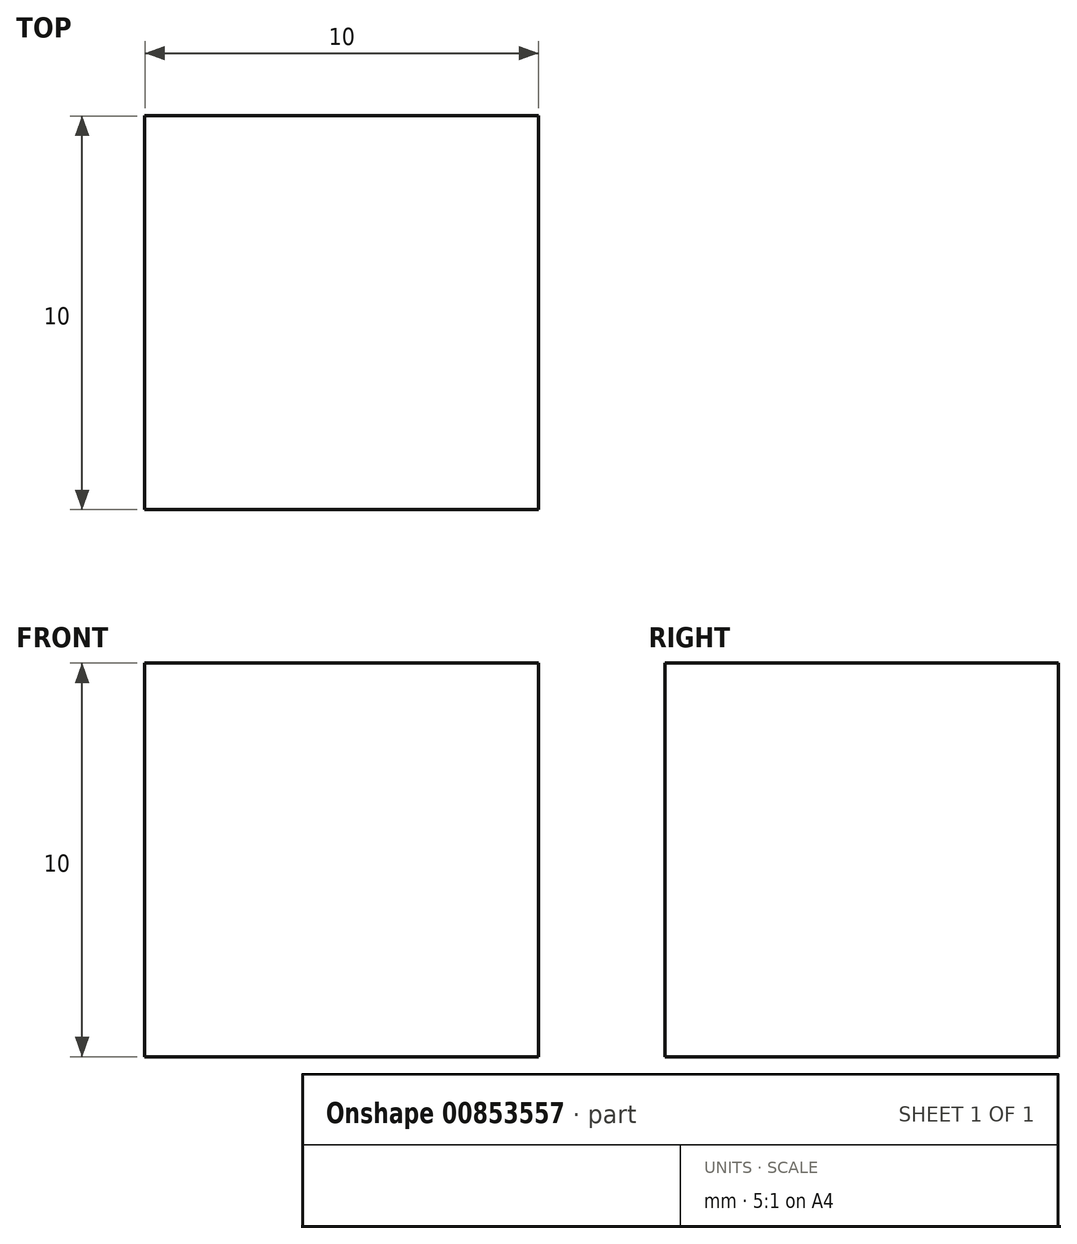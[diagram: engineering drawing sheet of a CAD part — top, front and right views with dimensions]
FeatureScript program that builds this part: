
annotation { "Feature Type Name" : "Feature", "Feature Type Description" : "" }
export const myFeature = defineFeature(function(context is Context, id is Id, definition is map)
    precondition{}
    {
        {
            var Q0;
            Q0=qCreatedBy(makeId("Top.planeOp"),FACE);
            var sketch = newSketch(context, id + "F0", { "sketchPlane" : qUnion([Q0])});
            skLineSegment(sketch, "E0.bottom", {"start": v(1.32, 0.81) * mm, "end": v(11.32, 0.81) * mm});
            skLineSegment(sketch, "E0.top", {"start": v(1.32, -9.19) * mm, "end": v(11.32, -9.19) * mm});
            skLineSegment(sketch, "E0.left", {"start": v(1.32, 0.81) * mm, "end": v(1.32, -9.19) * mm});
            skLineSegment(sketch, "E0.right", {"start": v(11.32, 0.81) * mm, "end": v(11.32, -9.19) * mm});
            skSolve(sketch);
        }
        {
            var Q0;
            Q0=makeQuery(id+"F0.imprint","IMPRINT",FACE,{"disambiguationData":[TD([[makeQuery(id+"F0.imprint","IMPRINT",EDGE,{"derivedFrom":sQuery(id+"F0.wireOp",EDGE,"E0.bottom")}),-1.0]])]});
            extrude(context, id + "F1", {"entities" : qUnion([Q0]), "depth" : 10 * mm, "offsetDistance" : 25 * mm});
        }
    });
